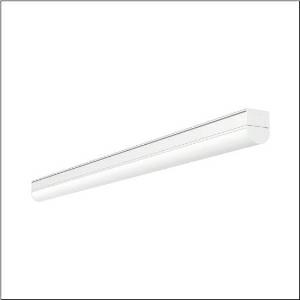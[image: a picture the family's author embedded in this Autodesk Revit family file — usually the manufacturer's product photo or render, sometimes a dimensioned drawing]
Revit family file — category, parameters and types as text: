
# Revit family: ecopack_r__31_51lj12dnm80a_c0ee
name_source: partatom
category: Lighting Fixtures
units: mm (PartAtom-declared; Revit-internal decimal feet)

## family parameters
Cut with Voids When Loaded = No
Host = Face
Light Source = No
Part Type = Normal
Room Calculation Point = No
Round Connector Dimension = Use Diameter
Shared = No

## types (1)
- --- (1 x LED, 6780 lm, 52 W, 5000K)
    Apparent Load = 52 VA
    CIE Flux Codes = 39 67 87 89 100
    Color Rendering = 80
    Color Temperature = 5000K
    Default Elevation = 1800 mm
    Description = Ecopack® 31, diffuser luminaire, primary optical cover: cover, of PC, frosted, light emission: direct distribution, primary light characteristic: symmetric, installation type: surface-mounted, LED, rated luminous flux: 7.000lm, luminous efficacy: 135lm/W, light colour: 830/840/850, colour temperature: 3000/4000/5000K, control gear: ECG DALI, with terminal, 5-pole, mains connection: 220..240V, AC, 50/60Hz, rated input power: 52W, housing, of aluminium, traffic white (RAL 9016), length: 1.450mm, width: 56mm, height: 68mm, end cap, of PC, white, protection rating (complete): IP20, insulation class (complete): insulation class I (protective earthing), certification: CE, impact resistance: IK06, permissible operating ambient temperature: -20..+40°C, packaging unit: 1 piece
    Height = 68 mm
    Lamp = 1 x LED
    Lamp Light Flux = 6780 lm
    Lamp Power = 52 W
    Lamp count = 1
    Length = 1450 mm
    Luminous efficacy = 130 lm/W
    Manufacturer = Siteco
    ModVariant = No
    Model = 51LJ12DNM80A
    Mounting Place = Ceiling
    Mounting Type = Surface mounted
    Number of Poles = 1
    OnlyDefault = Yes
    Power Factor = 1
    Product Name = Ecopack® 31
    Product group = diffuser luminaire
    ProductGroupID = 303
    Protection Class = Protection class I
    Protection Degree = IP 20
    RLX_Detail_Level = 1
    RlxData = <blob elided: 21745 chars, md5=639c9ab5>
    Socket = socket
    Standby Power = 0 W
    System Light Flux = 6780 lm
    System Power = 52 W
    Type Comments = individual setting: colour temperature 5000K
    Type Image = l_1007033.jpg
    URL = http://relux.com
    VarID = @adj_086269
    Voltage = 0 V
    Weight = 0.00 kg
    Width = 56 mm

## geometry (parser evidence)
native form markers: Blend x4, Sweep x16
no freeform markers — native parametric forms only
